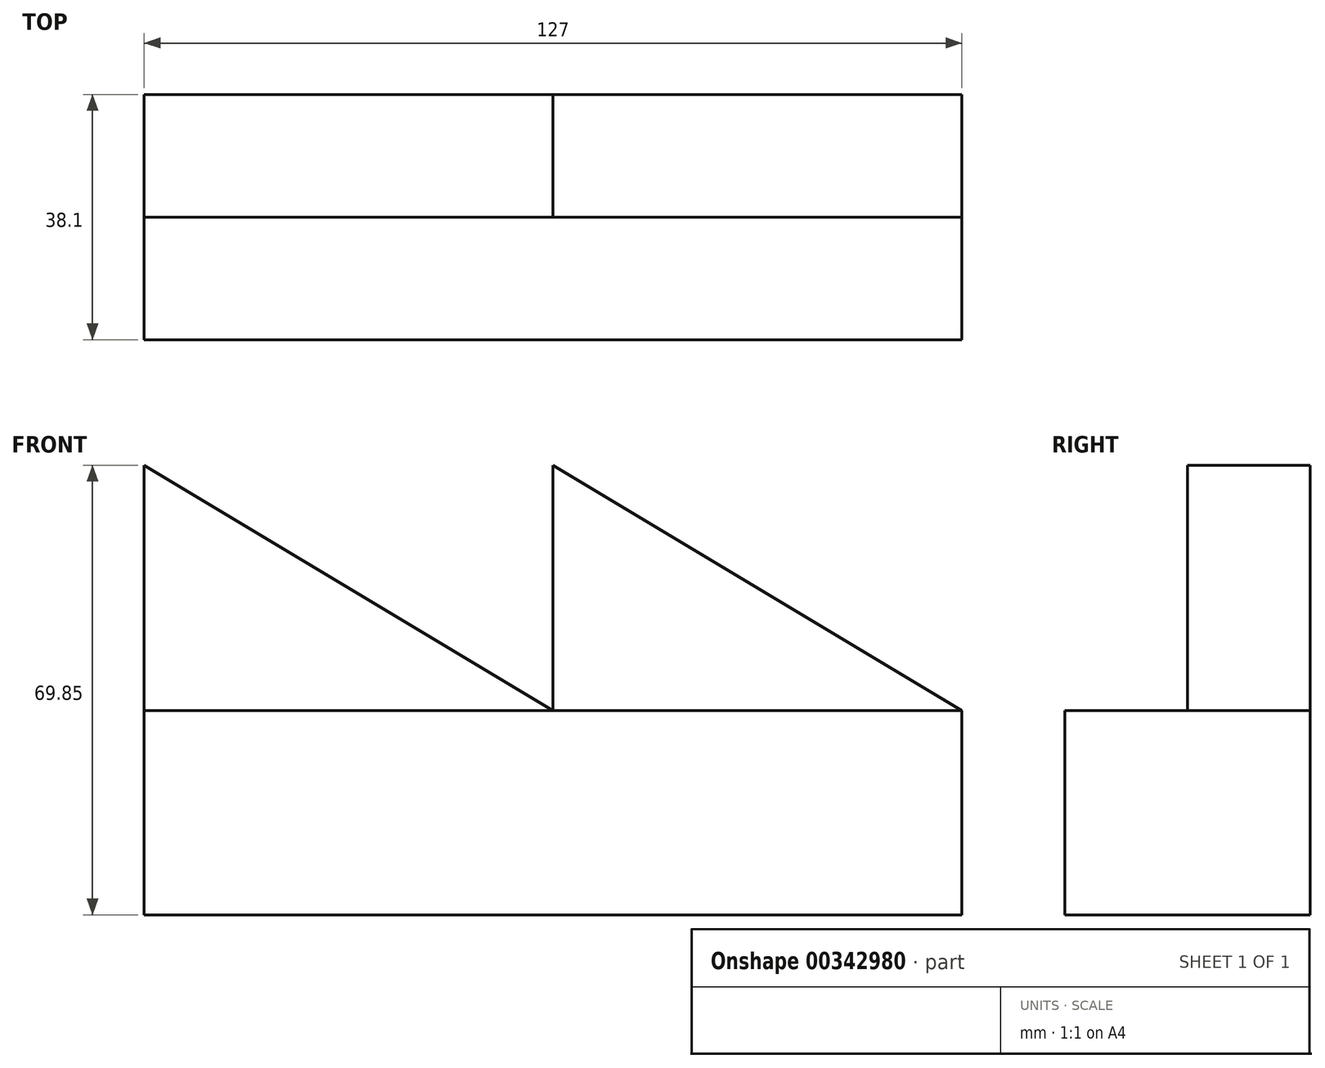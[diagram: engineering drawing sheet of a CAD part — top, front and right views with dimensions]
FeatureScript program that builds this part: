
annotation { "Feature Type Name" : "Feature", "Feature Type Description" : "" }
export const myFeature = defineFeature(function(context is Context, id is Id, definition is map)
    precondition{}
    {
        {
            var Q0;
            Q0=qCreatedBy(makeId("Front.planeOp"),FACE);
            var sketch = newSketch(context, id + "F0", { "sketchPlane" : qUnion([Q0])});
            skLineSegment(sketch, "E0", {"start": v(-63.5, -31.75) * mm, "end": v(63.5, -31.75) * mm});
            skLineSegment(sketch, "E1", {"start": v(63.5, -31.75) * mm, "end": v(63.5, 0) * mm});
            skLineSegment(sketch, "E2", {"start": v(-63.5, -31.75) * mm, "end": v(-63.5, 0) * mm});
            skLineSegment(sketch, "E3", {"start": v(-63.5, 0) * mm, "end": v(63.5, 0) * mm});
            skLineSegment(sketch, "E4", {"start": v(-63.5, 0) * mm, "end": v(-63.5, 38.1) * mm});
            skLineSegment(sketch, "E5", {"start": v(0, 38.1) * mm, "end": v(0, 0) * mm});
            skLineSegment(sketch, "E6", {"start": v(-63.5, 38.1) * mm, "end": v(0, 0) * mm});
            skLineSegment(sketch, "E7", {"start": v(0, 38.1) * mm, "end": v(63.5, 0) * mm});
            skSolve(sketch);
        }
        {
            var Q0;
            Q0=makeQuery(id+"F0.imprint","IMPRINT",FACE,{"disambiguationData":[TD([[makeQuery(id+"F0.imprint","IMPRINT",EDGE,{"derivedFrom":sQuery(id+"F0.wireOp",EDGE,"E0")}),1.0]])]});
            extrude(context, id + "F1", {"entities" : qUnion([Q0]), "depth" : 38.1 * mm});
        }
        {
            var Q0;
            {var subQ0=sQuery(id+"F0.wireOp",EDGE,"E4");Q0=makeQuery(id+"F0.imprint","IMPRINT",FACE,{"disambiguationData":[TD([[makeQuery(id+"F0.imprint","IMPRINT",EDGE,{"derivedFrom":subQ0}),-1.0]])]});}
            var Q1;
            {var subQ2=sQuery(id+"F0.wireOp",EDGE,"E5");Q1=makeQuery(id+"F0.imprint","IMPRINT",FACE,{"disambiguationData":[TD([[makeQuery(id+"F0.imprint","IMPRINT",EDGE,{"derivedFrom":subQ2}),1.0]])]});}
            extrude(context, id + "F2", {"entities" : qUnion([Q0, Q1]), "operationType" : NewBodyOperationType.ADD, "depth" : 19.05 * mm});
        }
    });
